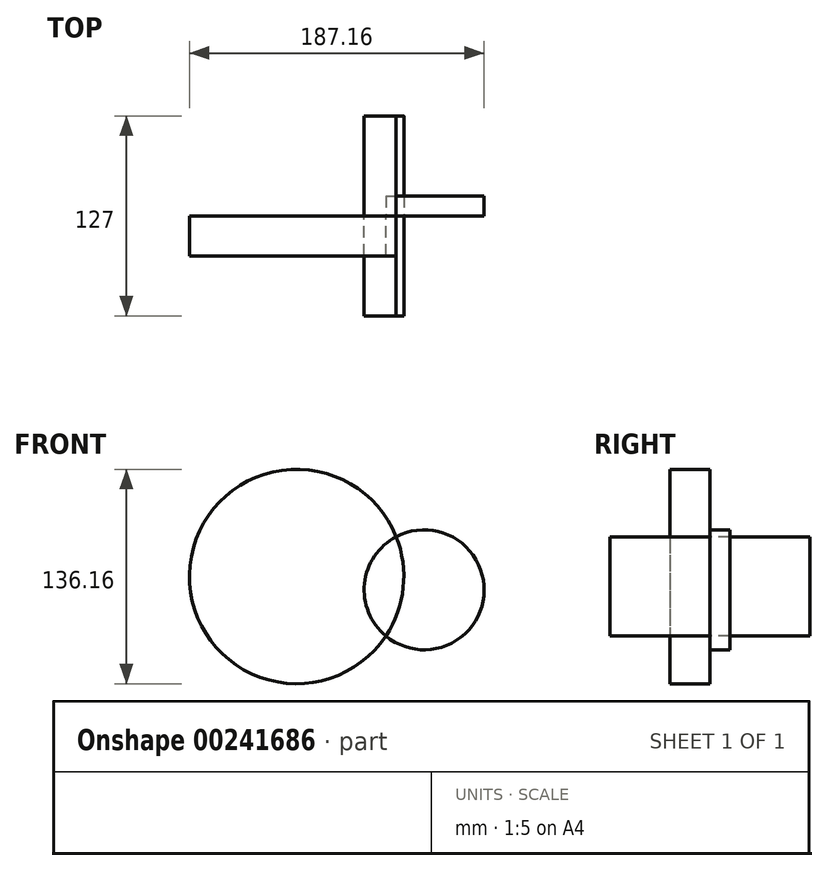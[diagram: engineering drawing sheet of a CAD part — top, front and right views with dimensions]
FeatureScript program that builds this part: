
annotation { "Feature Type Name" : "Feature", "Feature Type Description" : "" }
export const myFeature = defineFeature(function(context is Context, id is Id, definition is map)
    precondition{}
    {
        {
            var Q0;
            Q0=qCreatedBy(makeId("Front.planeOp"),FACE);
            var sketch = newSketch(context, id + "F0", { "sketchPlane" : qUnion([Q0])});
            skCircle(sketch, "E0", {"center": v(0, 0) * mm, "radius": 38.1 * mm});
            skCircle(sketch, "E1", {"center": v(-80.98, 8.47) * mm, "radius": 68.08 * mm});
            skSolve(sketch);
        }
        {
            var Q0;
            {var subQ0=sQuery(id+"F0.wireOp",EDGE,"E1");var subQ1=sQuery(id+"F0.wireOp",EDGE,"E0");var subQ2=makeQuery(id+"F0.imprint","INTERSECT",VERTEX,{"disambiguationData":[OD(0.0)],"derivedFrom":[subQ1,subQ0]});Q0=makeQuery(id+"F0.imprint","IMPRINT",FACE,{"disambiguationData":[TD([[makeQuery(id+"F0.imprint","IMPRINT",EDGE,{"disambiguationData":[TD([[subQ2,1.0]])],"derivedFrom":subQ1}),-1.0]])]});}
            extrude(context, id + "F1", {"entities" : qUnion([Q0]), "depth" : 25.4 * mm});
        }
        {
            var Q0;
            {var subQ0=sQuery(id+"F0.wireOp",EDGE,"E1");var subQ1=sQuery(id+"F0.wireOp",EDGE,"E0");var subQ2=makeQuery(id+"F0.imprint","INTERSECT",VERTEX,{"disambiguationData":[OD(0.0)],"derivedFrom":[subQ1,subQ0]});Q0=makeQuery(id+"F0.imprint","IMPRINT",FACE,{"disambiguationData":[TD([[makeQuery(id+"F0.imprint","IMPRINT",EDGE,{"disambiguationData":[TD([[subQ2,-1.0]])],"derivedFrom":subQ1}),1.0]])]});}
            extrude(context, id + "F2", {"entities" : qUnion([Q0]), "oppositeDirection" : true, "depth" : 12.7 * mm});
        }
        {
            var Q0;
            {var subQ0=sQuery(id+"F0.wireOp",EDGE,"E1");var subQ1=sQuery(id+"F0.wireOp",EDGE,"E0");var subQ2=makeQuery(id+"F0.imprint","INTERSECT",VERTEX,{"disambiguationData":[OD(0.0)],"derivedFrom":[subQ1,subQ0]});Q0=makeQuery(id+"F0.imprint","IMPRINT",FACE,{"disambiguationData":[TD([[makeQuery(id+"F0.imprint","IMPRINT",EDGE,{"disambiguationData":[TD([[subQ2,1.0]])],"derivedFrom":subQ1}),1.0]])]});}
            extrude(context, id + "F3", {"entities" : qUnion([Q0]), "depth" : 63.5 * mm, "hasSecondDirection" : true, "secondDirectionOppositeDirection" : true, "secondDirectionDepth" : 63.5 * mm});
        }
    });
